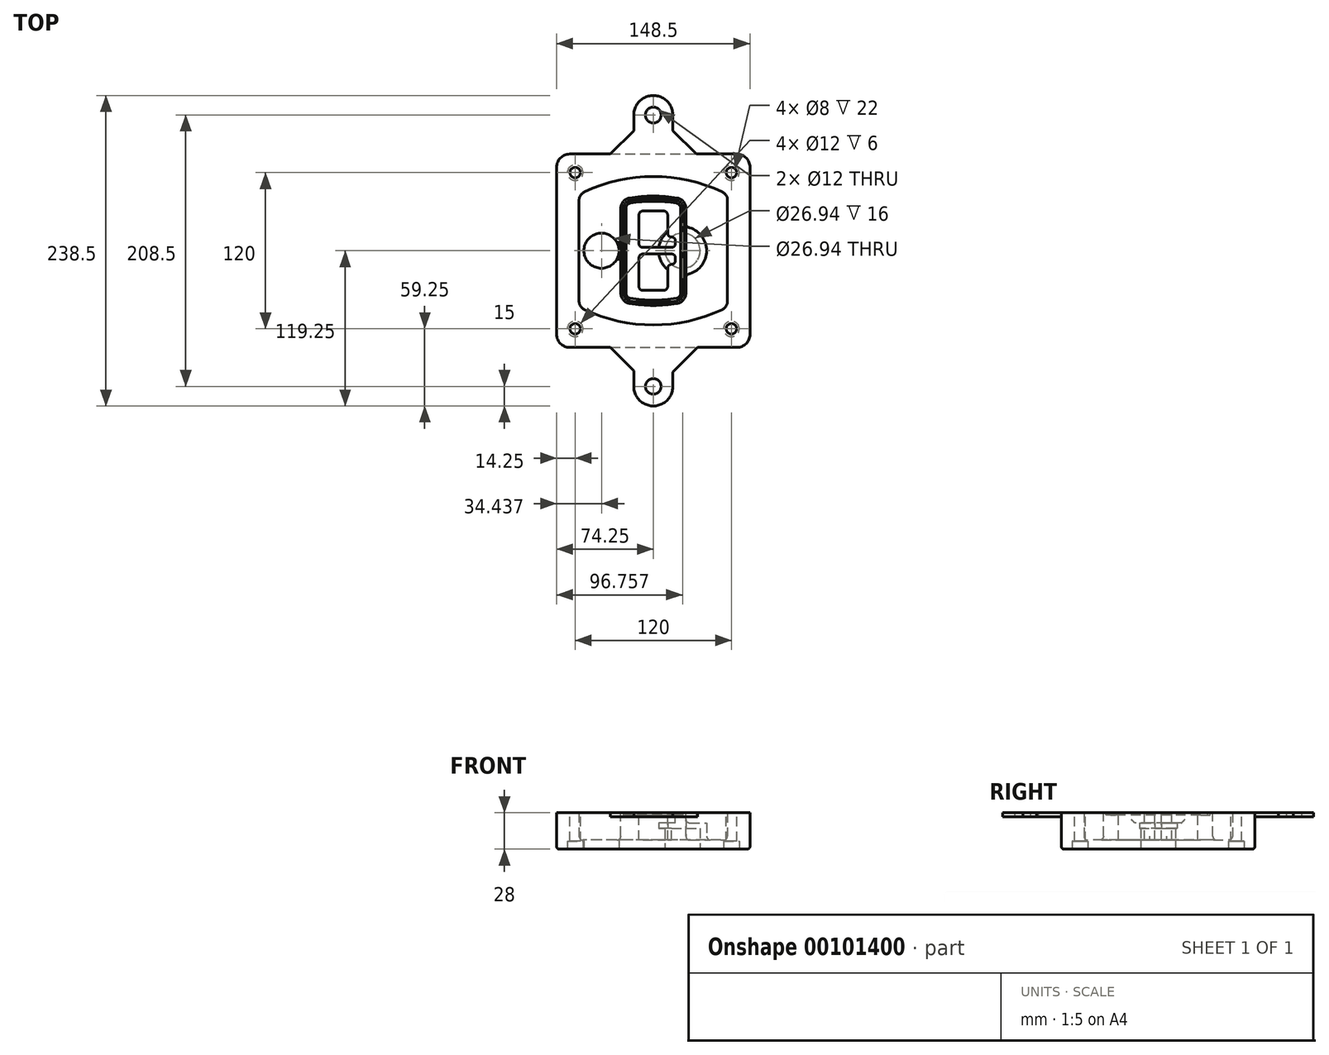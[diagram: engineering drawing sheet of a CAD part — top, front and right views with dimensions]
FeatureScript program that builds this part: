
annotation { "Feature Type Name" : "Feature", "Feature Type Description" : "" }
export const myFeature = defineFeature(function(context is Context, id is Id, definition is map)
    precondition{}
    {
        {
            var Q0;
            Q0=qCreatedBy(makeId("Top.planeOp"),FACE);
            var sketch = newSketch(context, id + "F0", { "sketchPlane" : qUnion([Q0])});
            skPoint(sketch, "E0.rect.middle", {"position": v(0, 0) * mm});
            skLineSegment(sketch, "E1.bottom", {"start": v(-64.25, -74.25) * mm, "end": v(64.25, -74.25) * mm});
            skLineSegment(sketch, "E1.top", {"start": v(-64.25, 74.25) * mm, "end": v(64.25, 74.25) * mm});
            skLineSegment(sketch, "E1.left", {"start": v(-74.25, -64.25) * mm, "end": v(-74.25, 64.25) * mm});
            skLineSegment(sketch, "E1.right", {"start": v(74.25, -64.25) * mm, "end": v(74.25, 64.25) * mm});
            skLineSegment(sketch, "E2", {"start": v(-74.25, 74.25) * mm, "end": v(74.25, -74.25) * mm, "construction": true});
            skLineSegment(sketch, "E3", {"start": v(74.25, 74.25) * mm, "end": v(-74.25, -74.25) * mm, "construction": true});
            skCircle(sketch, "E4", {"center": v(-60, 60) * mm, "radius": 4 * mm});
            skCircle(sketch, "E5", {"center": v(60, 60) * mm, "radius": 4 * mm});
            skCircle(sketch, "E6", {"center": v(60, -60) * mm, "radius": 4 * mm});
            skCircle(sketch, "E7", {"center": v(-60, -60) * mm, "radius": 4 * mm});
            skLineSegment(sketch, "E8", {"start": v(-60, 60) * mm, "end": v(60, 60) * mm, "construction": true});
            skLineSegment(sketch, "E9", {"start": v(60, 60) * mm, "end": v(60, -60) * mm, "construction": true});
            skLineSegment(sketch, "E10", {"start": v(60, -60) * mm, "end": v(-60, -60) * mm, "construction": true});
            skLineSegment(sketch, "E11", {"start": v(-60, -60) * mm, "end": v(-60, 60) * mm, "construction": true});
            skLineSegment(sketch, "E12", {"start": v(-60, 38.83) * mm, "end": v(-60, -38.83) * mm});
            skLineSegment(sketch, "E13", {"start": v(60, 38.83) * mm, "end": v(60, -38.83) * mm});
            skArc(sketch, "E14", {"start": v(54.26, 47.88) * mm, "mid": v(0, 60) * mm, "end": v(-54.26, 47.88) * mm});
            skArc(sketch, "E15", {"start": v(-54.26, -47.88) * mm, "mid": v(0, -60) * mm, "end": v(54.26, -47.88) * mm});
            skLineSegment(sketch, "E16", {"start": v(-60, 0) * mm, "end": v(60, 0) * mm, "construction": true});
            skPoint(sketch, "E17.visualSharp", {"position": v(-60, -45) * mm});
            skArc(sketch, "E17.filletArc", {"start": v(-60, -38.83) * mm, "mid": v(-58.44, -44.2) * mm, "end": v(-54.26, -47.88) * mm});
            skPoint(sketch, "E18.visualSharp", {"position": v(-60, 45) * mm});
            skArc(sketch, "E18.filletArc", {"start": v(-54.26, 47.88) * mm, "mid": v(-58.44, 44.2) * mm, "end": v(-60, 38.83) * mm});
            skPoint(sketch, "E19.visualSharp", {"position": v(60, 45) * mm});
            skArc(sketch, "E19.filletArc", {"start": v(60, 38.83) * mm, "mid": v(58.44, 44.2) * mm, "end": v(54.26, 47.88) * mm});
            skPoint(sketch, "E20.visualSharp", {"position": v(60, -45) * mm});
            skArc(sketch, "E20.filletArc", {"start": v(54.26, -47.88) * mm, "mid": v(58.44, -44.2) * mm, "end": v(60, -38.83) * mm});
            skPoint(sketch, "E21.visualSharp", {"position": v(-74.25, 74.25) * mm});
            skArc(sketch, "E21.filletArc", {"start": v(-64.25, 74.25) * mm, "mid": v(-71.32, 71.32) * mm, "end": v(-74.25, 64.25) * mm});
            skPoint(sketch, "E22.visualSharp", {"position": v(74.25, 74.25) * mm});
            skArc(sketch, "E22.filletArc", {"start": v(74.25, 64.25) * mm, "mid": v(71.32, 71.32) * mm, "end": v(64.25, 74.25) * mm});
            skPoint(sketch, "E23.visualSharp", {"position": v(74.25, -74.25) * mm});
            skArc(sketch, "E23.filletArc", {"start": v(64.25, -74.25) * mm, "mid": v(71.32, -71.32) * mm, "end": v(74.25, -64.25) * mm});
            skPoint(sketch, "E24.visualSharp", {"position": v(-74.25, -74.25) * mm});
            skArc(sketch, "E24.filletArc", {"start": v(-74.25, -64.25) * mm, "mid": v(-71.32, -71.32) * mm, "end": v(-64.25, -74.25) * mm});
            skArc(sketch, "E25.0", {"start": v(57, 38.83) * mm, "mid": v(55.9, 42.58) * mm, "end": v(52.98, 45.17) * mm});
            skLineSegment(sketch, "E25.1", {"start": v(57, 38.83) * mm, "end": v(57, -38.83) * mm});
            skArc(sketch, "E25.2", {"start": v(52.98, -45.17) * mm, "mid": v(55.9, -42.58) * mm, "end": v(57, -38.83) * mm});
            skArc(sketch, "E25.3", {"start": v(-52.98, -45.17) * mm, "mid": v(0, -57) * mm, "end": v(52.98, -45.17) * mm});
            skArc(sketch, "E25.4", {"start": v(-57, -38.83) * mm, "mid": v(-55.9, -42.58) * mm, "end": v(-52.98, -45.17) * mm});
            skArc(sketch, "E25.5", {"start": v(52.98, 45.17) * mm, "mid": v(0, 57) * mm, "end": v(-52.98, 45.17) * mm});
            skLineSegment(sketch, "E25.6", {"start": v(-57, 38.83) * mm, "end": v(-57, -38.83) * mm});
            skArc(sketch, "E25.7", {"start": v(-52.98, 45.17) * mm, "mid": v(-55.9, 42.58) * mm, "end": v(-57, 38.83) * mm});
            skArc(sketch, "E26.0", {"start": v(-55.96, 51.5) * mm, "mid": v(-61.82, 46.33) * mm, "end": v(-64, 38.83) * mm});
            skArc(sketch, "E26.1", {"start": v(55.96, 51.5) * mm, "mid": v(0, 64) * mm, "end": v(-55.96, 51.5) * mm});
            skArc(sketch, "E26.2", {"start": v(64, 38.83) * mm, "mid": v(61.82, 46.33) * mm, "end": v(55.96, 51.5) * mm});
            skLineSegment(sketch, "E26.3", {"start": v(64, 38.83) * mm, "end": v(64, -38.83) * mm});
            skArc(sketch, "E26.4", {"start": v(55.96, -51.5) * mm, "mid": v(61.82, -46.33) * mm, "end": v(64, -38.83) * mm});
            skLineSegment(sketch, "E26.5", {"start": v(-64, 38.83) * mm, "end": v(-64, -38.83) * mm});
            skArc(sketch, "E26.6", {"start": v(-55.96, -51.5) * mm, "mid": v(0, -64) * mm, "end": v(55.96, -51.5) * mm});
            skArc(sketch, "E26.7", {"start": v(-64, -38.83) * mm, "mid": v(-61.82, -46.33) * mm, "end": v(-55.96, -51.5) * mm});
            skSolve(sketch);
        }
        {
            var Q0;
            Q0=makeQuery(id+"F0.imprint","IMPRINT",FACE,{"disambiguationData":[TD([[makeQuery(id+"F0.imprint","IMPRINT",EDGE,{"derivedFrom":sQuery(id+"F0.wireOp",EDGE,"E1.bottom")}),1.0]])]});
            var Q1;
            Q1=makeQuery(id+"F0.imprint","IMPRINT",FACE,{"disambiguationData":[TD([[makeQuery(id+"F0.imprint","IMPRINT",EDGE,{"derivedFrom":sQuery(id+"F0.wireOp",EDGE,"E12")}),1.0]])]});
            var Q2;
            Q2=makeQuery(id+"F0.imprint","IMPRINT",FACE,{"disambiguationData":[TD([[makeQuery(id+"F0.imprint","IMPRINT",EDGE,{"derivedFrom":sQuery(id+"F0.wireOp",EDGE,"E25.0")}),1.0]])]});
            var Q3;
            Q3=makeQuery(id+"F0.imprint","IMPRINT",FACE,{"disambiguationData":[TD([[makeQuery(id+"F0.imprint","IMPRINT",EDGE,{"derivedFrom":sQuery(id+"F0.wireOp",EDGE,"E12")}),-1.0]])]});
            extrude(context, id + "F1", {"entities" : qUnion([Q0, Q1, Q2, Q3]), "oppositeDirection" : true, "depth" : 25 * mm});
        }
        {
            var Q0;
            Q0=makeQuery(id+"F0.imprint","IMPRINT",FACE,{"disambiguationData":[TD([[makeQuery(id+"F0.imprint","IMPRINT",EDGE,{"derivedFrom":sQuery(id+"F0.wireOp",EDGE,"E12")}),1.0]])]});
            extrude(context, id + "F2", {"entities" : qUnion([Q0]), "operationType" : NewBodyOperationType.ADD, "depth" : 3 * mm});
        }
        {
            var Q0;
            Q0=makeQuery(id+"F0.imprint","IMPRINT",FACE,{"disambiguationData":[TD([[makeQuery(id+"F0.imprint","IMPRINT",EDGE,{"derivedFrom":sQuery(id+"F0.wireOp",EDGE,"E25.0")}),1.0]])]});
            extrude(context, id + "F3", {"entities" : qUnion([Q0]), "operationType" : NewBodyOperationType.REMOVE, "oppositeDirection" : true, "depth" : 18 * mm});
        }
        {
            var Q0;
            Q0=makeQuery(id+"F2.opExtrude","CAP_FACE",FACE,{"disambiguationData":[OSD([sQuery(id+"F0.wireOp",EDGE,"E12"),sQuery(id+"F0.wireOp",EDGE,"E13"),sQuery(id+"F0.wireOp",EDGE,"E14"),sQuery(id+"F0.wireOp",EDGE,"E15"),sQuery(id+"F0.wireOp",EDGE,"E17.filletArc"),sQuery(id+"F0.wireOp",EDGE,"E18.filletArc"),sQuery(id+"F0.wireOp",EDGE,"E19.filletArc"),sQuery(id+"F0.wireOp",EDGE,"E20.filletArc"),sQuery(id+"F0.wireOp",EDGE,"E25.0"),sQuery(id+"F0.wireOp",EDGE,"E25.1"),sQuery(id+"F0.wireOp",EDGE,"E25.2"),sQuery(id+"F0.wireOp",EDGE,"E25.3"),sQuery(id+"F0.wireOp",EDGE,"E25.4"),sQuery(id+"F0.wireOp",EDGE,"E25.5"),sQuery(id+"F0.wireOp",EDGE,"E25.6"),sQuery(id+"F0.wireOp",EDGE,"E25.7")])],"isStart":false});
            var sketch = newSketch(context, id + "F4", { "sketchPlane" : qUnion([Q0])});
            skArc(sketch, "E27.0", {"start": v(-18.34, -40.45) * mm, "mid": v(0, -42) * mm, "end": v(18.34, -40.45) * mm});
            skArc(sketch, "E28.0", {"start": v(18.34, 40.45) * mm, "mid": v(0, 42) * mm, "end": v(-18.34, 40.45) * mm});
            skLineSegment(sketch, "E29", {"start": v(-25, 32.57) * mm, "end": v(-25, -32.57) * mm});
            skLineSegment(sketch, "E30", {"start": v(25, 32.57) * mm, "end": v(25, -32.57) * mm});
            skLineSegment(sketch, "E31", {"start": v(-25, 39.1) * mm, "end": v(25, 39.1) * mm, "construction": true});
            skLineSegment(sketch, "E32", {"start": v(-25, -39.1) * mm, "end": v(25, -39.1) * mm, "construction": true});
            skPoint(sketch, "E33.visualSharp", {"position": v(-25, 39.1) * mm});
            skArc(sketch, "E33.filletArc", {"start": v(-18.34, 40.45) * mm, "mid": v(-23.11, 37.73) * mm, "end": v(-25, 32.57) * mm});
            skPoint(sketch, "E34.visualSharp", {"position": v(25, 39.1) * mm});
            skArc(sketch, "E34.filletArc", {"start": v(25, 32.57) * mm, "mid": v(23.11, 37.73) * mm, "end": v(18.34, 40.45) * mm});
            skPoint(sketch, "E35.visualSharp", {"position": v(25, -39.1) * mm});
            skArc(sketch, "E35.filletArc", {"start": v(18.34, -40.45) * mm, "mid": v(23.11, -37.73) * mm, "end": v(25, -32.57) * mm});
            skPoint(sketch, "E36.visualSharp", {"position": v(-25, -39.1) * mm});
            skArc(sketch, "E36.filletArc", {"start": v(-25, -32.57) * mm, "mid": v(-23.11, -37.73) * mm, "end": v(-18.34, -40.45) * mm});
            skArc(sketch, "E37.0", {"start": v(52.98, 45.17) * mm, "mid": v(0, 57) * mm, "end": v(-52.98, 45.17) * mm});
            skArc(sketch, "E37.1", {"start": v(-52.98, 45.17) * mm, "mid": v(-55.9, 42.58) * mm, "end": v(-57, 38.83) * mm});
            skLineSegment(sketch, "E37.2", {"start": v(-57, 38.83) * mm, "end": v(-57, -38.83) * mm});
            skArc(sketch, "E37.3", {"start": v(-57, -38.83) * mm, "mid": v(-55.9, -42.58) * mm, "end": v(-52.98, -45.17) * mm});
            skArc(sketch, "E37.4", {"start": v(-52.98, -45.17) * mm, "mid": v(0, -57) * mm, "end": v(52.98, -45.17) * mm});
            skArc(sketch, "E37.5", {"start": v(52.98, -45.17) * mm, "mid": v(55.9, -42.58) * mm, "end": v(57, -38.83) * mm});
            skLineSegment(sketch, "E37.6", {"start": v(57, 38.83) * mm, "end": v(57, -38.83) * mm});
            skArc(sketch, "E37.7", {"start": v(57, 38.83) * mm, "mid": v(55.9, 42.58) * mm, "end": v(52.98, 45.17) * mm});
            skLineSegment(sketch, "E38.0", {"start": v(23, 32.57) * mm, "end": v(23, -32.57) * mm});
            skArc(sketch, "E38.1", {"start": v(18, -38.48) * mm, "mid": v(21.58, -36.44) * mm, "end": v(23, -32.57) * mm});
            skArc(sketch, "E38.2", {"start": v(-18, -38.48) * mm, "mid": v(0, -40) * mm, "end": v(18, -38.48) * mm});
            skArc(sketch, "E38.3", {"start": v(-23, -32.57) * mm, "mid": v(-21.58, -36.44) * mm, "end": v(-18, -38.48) * mm});
            skLineSegment(sketch, "E38.4", {"start": v(-23, 32.57) * mm, "end": v(-23, -32.57) * mm});
            skArc(sketch, "E38.5", {"start": v(23, 32.57) * mm, "mid": v(21.58, 36.44) * mm, "end": v(18, 38.48) * mm});
            skArc(sketch, "E38.6", {"start": v(-18, 38.48) * mm, "mid": v(-21.58, 36.44) * mm, "end": v(-23, 32.57) * mm});
            skArc(sketch, "E38.7", {"start": v(18, 38.48) * mm, "mid": v(0, 40) * mm, "end": v(-18, 38.48) * mm});
            skArc(sketch, "E39.0", {"start": v(21, 32.57) * mm, "mid": v(20.06, 35.15) * mm, "end": v(17.67, 36.5) * mm});
            skLineSegment(sketch, "E39.1", {"start": v(21, 32.57) * mm, "end": v(21, -32.57) * mm});
            skArc(sketch, "E39.2", {"start": v(17.67, -36.5) * mm, "mid": v(20.06, -35.15) * mm, "end": v(21, -32.57) * mm});
            skArc(sketch, "E39.3", {"start": v(-17.67, -36.5) * mm, "mid": v(0, -38) * mm, "end": v(17.67, -36.5) * mm});
            skArc(sketch, "E39.4", {"start": v(-21, -32.57) * mm, "mid": v(-20.06, -35.15) * mm, "end": v(-17.67, -36.5) * mm});
            skArc(sketch, "E39.5", {"start": v(17.67, 36.5) * mm, "mid": v(0, 38) * mm, "end": v(-17.67, 36.5) * mm});
            skLineSegment(sketch, "E39.6", {"start": v(-21, 32.57) * mm, "end": v(-21, -32.57) * mm});
            skArc(sketch, "E39.7", {"start": v(-17.67, 36.5) * mm, "mid": v(-20.06, 35.15) * mm, "end": v(-21, 32.57) * mm});
            skLineSegment(sketch, "E40", {"start": v(-25, 0) * mm, "end": v(25, 0) * mm, "construction": true});
            skLineSegment(sketch, "E41", {"start": v(-11, 5.5) * mm, "end": v(-11, 27.5) * mm});
            skLineSegment(sketch, "E42", {"start": v(-8, 30.5) * mm, "end": v(8, 30.5) * mm});
            skLineSegment(sketch, "E43", {"start": v(11, 27.5) * mm, "end": v(11, 13.5) * mm});
            skLineSegment(sketch, "E44", {"start": v(14, 10.5) * mm, "end": v(14, 10.5) * mm});
            skLineSegment(sketch, "E45", {"start": v(17, 7.5) * mm, "end": v(17, 5.5) * mm});
            skLineSegment(sketch, "E46", {"start": v(14, 2.5) * mm, "end": v(-8, 2.5) * mm});
            skPoint(sketch, "E47.visualSharp", {"position": v(-11, 30.5) * mm});
            skArc(sketch, "E47.filletArc", {"start": v(-8, 30.5) * mm, "mid": v(-10.12, 29.62) * mm, "end": v(-11, 27.5) * mm});
            skPoint(sketch, "E48.visualSharp", {"position": v(11, 30.5) * mm});
            skArc(sketch, "E48.filletArc", {"start": v(11, 27.5) * mm, "mid": v(10.12, 29.62) * mm, "end": v(8, 30.5) * mm});
            skPoint(sketch, "E49.visualSharp", {"position": v(11, 10.5) * mm});
            skArc(sketch, "E49.filletArc", {"start": v(11, 13.5) * mm, "mid": v(11.88, 11.38) * mm, "end": v(14, 10.5) * mm});
            skPoint(sketch, "E50.visualSharp", {"position": v(17, 10.5) * mm});
            skArc(sketch, "E50.filletArc", {"start": v(17, 7.5) * mm, "mid": v(16.12, 9.62) * mm, "end": v(14, 10.5) * mm});
            skPoint(sketch, "E51.visualSharp", {"position": v(17, 2.5) * mm});
            skArc(sketch, "E51.filletArc", {"start": v(14, 2.5) * mm, "mid": v(16.12, 3.38) * mm, "end": v(17, 5.5) * mm});
            skPoint(sketch, "E52.visualSharp", {"position": v(-11, 2.5) * mm});
            skArc(sketch, "E52.filletArc", {"start": v(-11, 5.5) * mm, "mid": v(-10.12, 3.38) * mm, "end": v(-8, 2.5) * mm});
            skLineSegment(sketch, "E53.0.MirrorCS", {"start": v(14, -2.5) * mm, "end": v(-8, -2.5) * mm});
            skArc(sketch, "E54.0.MirrorCS", {"start": v(-11, -5.5) * mm, "mid": v(-10.12, -3.38) * mm, "end": v(-8, -2.5) * mm});
            skLineSegment(sketch, "E55.0.MirrorCS", {"start": v(-11, -5.5) * mm, "end": v(-11, -27.5) * mm});
            skArc(sketch, "E56.0.MirrorCS", {"start": v(-8, -30.5) * mm, "mid": v(-10.12, -29.62) * mm, "end": v(-11, -27.5) * mm});
            skLineSegment(sketch, "E57.0.MirrorCS", {"start": v(-8, -30.5) * mm, "end": v(8, -30.5) * mm});
            skArc(sketch, "E58.0.MirrorCS", {"start": v(11, -27.5) * mm, "mid": v(10.12, -29.62) * mm, "end": v(8, -30.5) * mm});
            skLineSegment(sketch, "E59.0.MirrorCS", {"start": v(11, -27.5) * mm, "end": v(11, -13.5) * mm});
            skArc(sketch, "E60.0.MirrorCS", {"start": v(11, -13.5) * mm, "mid": v(11.88, -11.38) * mm, "end": v(14, -10.5) * mm});
            skArc(sketch, "E61.0.MirrorCS", {"start": v(17, -7.5) * mm, "mid": v(16.12, -9.62) * mm, "end": v(14, -10.5) * mm});
            skLineSegment(sketch, "E62.0.MirrorCS", {"start": v(17, -7.5) * mm, "end": v(17, -5.5) * mm});
            skArc(sketch, "E63.0.MirrorCS", {"start": v(14, -2.5) * mm, "mid": v(16.12, -3.38) * mm, "end": v(17, -5.5) * mm});
            skSolve(sketch);
        }
        {
            var Q0;
            Q0=makeQuery(id+"F4.imprint","IMPRINT",FACE,{"disambiguationData":[TD([[makeQuery(id+"F4.imprint","IMPRINT",EDGE,{"derivedFrom":sQuery(id+"F4.wireOp",EDGE,"E27.0")}),1.0]])]});
            var Q1;
            Q1=makeQuery(id+"F4.imprint","IMPRINT",FACE,{"disambiguationData":[TD([[makeQuery(id+"F4.imprint","IMPRINT",EDGE,{"derivedFrom":sQuery(id+"F4.wireOp",EDGE,"E38.0")}),-1.0]])]});
            var Q2;
            Q2=makeQuery(id+"F4.imprint","IMPRINT",FACE,{"disambiguationData":[TD([[makeQuery(id+"F4.imprint","IMPRINT",EDGE,{"derivedFrom":sQuery(id+"F4.wireOp",EDGE,"E39.0")}),1.0]])]});
            extrude(context, id + "F5", {"entities" : qUnion([Q0, Q1, Q2]), "operationType" : NewBodyOperationType.ADD, "endBound" : BoundingType.UP_TO_NEXT, "oppositeDirection" : true, "depth" : 25 * mm});
        }
        {
            var Q0;
            Q0=makeQuery(id+"F4.imprint","IMPRINT",FACE,{"disambiguationData":[TD([[makeQuery(id+"F4.imprint","IMPRINT",EDGE,{"derivedFrom":sQuery(id+"F4.wireOp",EDGE,"E38.0")}),-1.0]])]});
            extrude(context, id + "F6", {"entities" : qUnion([Q0]), "operationType" : NewBodyOperationType.REMOVE, "oppositeDirection" : true, "depth" : 2 * mm});
        }
        {
            var Q0;
            Q0=makeQuery(id+"F1.opExtrude","CAP_FACE",FACE,{"disambiguationData":[OSD([sQuery(id+"F0.wireOp",EDGE,"E1.bottom"),sQuery(id+"F0.wireOp",EDGE,"E1.top"),sQuery(id+"F0.wireOp",EDGE,"E1.left"),sQuery(id+"F0.wireOp",EDGE,"E1.right"),sQuery(id+"F0.wireOp",EDGE,"E4"),sQuery(id+"F0.wireOp",EDGE,"E5"),sQuery(id+"F0.wireOp",EDGE,"E6"),sQuery(id+"F0.wireOp",EDGE,"E7"),sQuery(id+"F0.wireOp",EDGE,"E21.filletArc"),sQuery(id+"F0.wireOp",EDGE,"E22.filletArc"),sQuery(id+"F0.wireOp",EDGE,"E23.filletArc"),sQuery(id+"F0.wireOp",EDGE,"E24.filletArc")])],"isStart":false});
            var sketch = newSketch(context, id + "F7", { "sketchPlane" : qUnion([Q0])});
            skCircle(sketch, "E64", {"center": v(22.5, 0) * mm, "radius": 13.47 * mm});
            skCircle(sketch, "E65", {"center": v(-39.81, 0) * mm, "radius": 13.47 * mm});
            skLineSegment(sketch, "E66", {"start": v(74.25, 0) * mm, "end": v(-74.25, 0) * mm});
            skCircle(sketch, "E67", {"center": v(22.5, 0) * mm, "radius": 18.47 * mm});
            skCircle(sketch, "E68", {"center": v(60, -60) * mm, "radius": 6 * mm});
            skCircle(sketch, "E69", {"center": v(-60, -60) * mm, "radius": 6 * mm});
            skCircle(sketch, "E70", {"center": v(-60, 60) * mm, "radius": 6 * mm});
            skCircle(sketch, "E71", {"center": v(60, 60) * mm, "radius": 6 * mm});
            skSolve(sketch);
        }
        {
            var Q0;
            {var subQ1=sQuery(id+"F7.wireOp",EDGE,"E66");var subQ4=sQuery(id+"F7.wireOp",EDGE,"E64");var subQ6=makeQuery(id+"F7.imprint","INTERSECT",VERTEX,{"disambiguationData":[OD(0.0)],"derivedFrom":[subQ4,subQ1]});Q0=makeQuery(id+"F7.imprint","IMPRINT",FACE,{"disambiguationData":[TD([[makeQuery(id+"F7.imprint","IMPRINT",EDGE,{"disambiguationData":[TD([[subQ6,-1.0]])],"derivedFrom":subQ4}),-1.0]])]});}
            var Q1;
            {var subQ0=sQuery(id+"F7.wireOp",EDGE,"E66");var subQ1=sQuery(id+"F7.wireOp",EDGE,"E64");var subQ3=makeQuery(id+"F7.imprint","INTERSECT",VERTEX,{"disambiguationData":[OD(0.0)],"derivedFrom":[subQ1,subQ0]});Q1=makeQuery(id+"F7.imprint","IMPRINT",FACE,{"disambiguationData":[TD([[makeQuery(id+"F7.imprint","IMPRINT",EDGE,{"disambiguationData":[TD([[subQ3,-1.0]])],"derivedFrom":subQ1}),1.0]])]});}
            var Q2;
            {var subQ0=sQuery(id+"F7.wireOp",EDGE,"E66");var subQ1=sQuery(id+"F7.wireOp",EDGE,"E64");var subQ3=makeQuery(id+"F7.imprint","INTERSECT",VERTEX,{"disambiguationData":[OD(0.0)],"derivedFrom":[subQ1,subQ0]});Q2=makeQuery(id+"F7.imprint","IMPRINT",FACE,{"disambiguationData":[TD([[makeQuery(id+"F7.imprint","IMPRINT",EDGE,{"disambiguationData":[TD([[subQ3,1.0]])],"derivedFrom":subQ1}),1.0]])]});}
            var Q3;
            {var subQ1=sQuery(id+"F7.wireOp",EDGE,"E66");var subQ4=sQuery(id+"F7.wireOp",EDGE,"E64");var subQ6=makeQuery(id+"F7.imprint","INTERSECT",VERTEX,{"disambiguationData":[OD(0.0)],"derivedFrom":[subQ4,subQ1]});Q3=makeQuery(id+"F7.imprint","IMPRINT",FACE,{"disambiguationData":[TD([[makeQuery(id+"F7.imprint","IMPRINT",EDGE,{"disambiguationData":[TD([[subQ6,1.0]])],"derivedFrom":subQ4}),-1.0]])]});}
            extrude(context, id + "F8", {"entities" : qUnion([Q0, Q1, Q2, Q3]), "operationType" : NewBodyOperationType.ADD, "oppositeDirection" : true, "depth" : 20 * mm});
        }
        {
            var Q0;
            {var subQ0=sQuery(id+"F7.wireOp",EDGE,"E66");var subQ1=sQuery(id+"F7.wireOp",EDGE,"E64");var subQ3=makeQuery(id+"F7.imprint","INTERSECT",VERTEX,{"disambiguationData":[OD(0.0)],"derivedFrom":[subQ1,subQ0]});Q0=makeQuery(id+"F7.imprint","IMPRINT",FACE,{"disambiguationData":[TD([[makeQuery(id+"F7.imprint","IMPRINT",EDGE,{"disambiguationData":[TD([[subQ3,-1.0]])],"derivedFrom":subQ1}),1.0]])]});}
            var Q1;
            {var subQ0=sQuery(id+"F7.wireOp",EDGE,"E66");var subQ1=sQuery(id+"F7.wireOp",EDGE,"E64");var subQ3=makeQuery(id+"F7.imprint","INTERSECT",VERTEX,{"disambiguationData":[OD(0.0)],"derivedFrom":[subQ1,subQ0]});Q1=makeQuery(id+"F7.imprint","IMPRINT",FACE,{"disambiguationData":[TD([[makeQuery(id+"F7.imprint","IMPRINT",EDGE,{"disambiguationData":[TD([[subQ3,1.0]])],"derivedFrom":subQ1}),1.0]])]});}
            extrude(context, id + "F9", {"entities" : qUnion([Q0, Q1]), "operationType" : NewBodyOperationType.REMOVE, "oppositeDirection" : true, "depth" : 16 * mm});
        }
        {
            var Q0;
            {var subQ0=sQuery(id+"F7.wireOp",EDGE,"E66");var subQ1=sQuery(id+"F7.wireOp",EDGE,"E65");var subQ3=makeQuery(id+"F7.imprint","INTERSECT",VERTEX,{"disambiguationData":[OD(0.0)],"derivedFrom":[subQ1,subQ0]});Q0=makeQuery(id+"F7.imprint","IMPRINT",FACE,{"disambiguationData":[TD([[makeQuery(id+"F7.imprint","IMPRINT",EDGE,{"disambiguationData":[TD([[subQ3,-1.0]])],"derivedFrom":subQ1}),1.0]])]});}
            var Q1;
            {var subQ0=sQuery(id+"F7.wireOp",EDGE,"E66");var subQ1=sQuery(id+"F7.wireOp",EDGE,"E65");var subQ3=makeQuery(id+"F7.imprint","INTERSECT",VERTEX,{"disambiguationData":[OD(0.0)],"derivedFrom":[subQ1,subQ0]});Q1=makeQuery(id+"F7.imprint","IMPRINT",FACE,{"disambiguationData":[TD([[makeQuery(id+"F7.imprint","IMPRINT",EDGE,{"disambiguationData":[TD([[subQ3,1.0]])],"derivedFrom":subQ1}),1.0]])]});}
            extrude(context, id + "F10", {"entities" : qUnion([Q0, Q1]), "operationType" : NewBodyOperationType.REMOVE, "oppositeDirection" : true, "depth" : 25 * mm});
        }
        {
            var Q0;
            Q0=makeQuery(id+"F7.imprint","IMPRINT",FACE,{"disambiguationData":[TD([[makeQuery(id+"F7.imprint","IMPRINT",EDGE,{"derivedFrom":sQuery(id+"F7.wireOp",EDGE,"E68")}),1.0]])]});
            var Q1;
            Q1=makeQuery(id+"F7.imprint","IMPRINT",FACE,{"disambiguationData":[TD([[makeQuery(id+"F7.imprint","IMPRINT",EDGE,{"derivedFrom":makeQuery(id+"F1.opExtrude","CAP_EDGE",EDGE,{"disambiguationData":[OSD([sQuery(id+"F0.wireOp",EDGE,"E5")])],"isStart":false})}),-1.0]])]});
            var Q2;
            Q2=makeQuery(id+"F7.imprint","IMPRINT",FACE,{"disambiguationData":[TD([[makeQuery(id+"F7.imprint","IMPRINT",EDGE,{"derivedFrom":sQuery(id+"F7.wireOp",EDGE,"E69")}),1.0]])]});
            var Q3;
            Q3=makeQuery(id+"F7.imprint","IMPRINT",FACE,{"disambiguationData":[TD([[makeQuery(id+"F7.imprint","IMPRINT",EDGE,{"derivedFrom":makeQuery(id+"F1.opExtrude","CAP_EDGE",EDGE,{"disambiguationData":[OSD([sQuery(id+"F0.wireOp",EDGE,"E4")])],"isStart":false})}),-1.0]])]});
            var Q4;
            Q4=makeQuery(id+"F7.imprint","IMPRINT",FACE,{"disambiguationData":[TD([[makeQuery(id+"F7.imprint","IMPRINT",EDGE,{"derivedFrom":sQuery(id+"F7.wireOp",EDGE,"E70")}),1.0]])]});
            var Q5;
            Q5=makeQuery(id+"F7.imprint","IMPRINT",FACE,{"disambiguationData":[TD([[makeQuery(id+"F7.imprint","IMPRINT",EDGE,{"derivedFrom":makeQuery(id+"F1.opExtrude","CAP_EDGE",EDGE,{"disambiguationData":[OSD([sQuery(id+"F0.wireOp",EDGE,"E7")])],"isStart":false})}),-1.0]])]});
            var Q6;
            Q6=makeQuery(id+"F7.imprint","IMPRINT",FACE,{"disambiguationData":[TD([[makeQuery(id+"F7.imprint","IMPRINT",EDGE,{"derivedFrom":sQuery(id+"F7.wireOp",EDGE,"E71")}),1.0]])]});
            var Q7;
            Q7=makeQuery(id+"F7.imprint","IMPRINT",FACE,{"disambiguationData":[TD([[makeQuery(id+"F7.imprint","IMPRINT",EDGE,{"derivedFrom":makeQuery(id+"F1.opExtrude","CAP_EDGE",EDGE,{"disambiguationData":[OSD([sQuery(id+"F0.wireOp",EDGE,"E6")])],"isStart":false})}),-1.0]])]});
            extrude(context, id + "F11", {"entities" : qUnion([Q0, Q1, Q2, Q3, Q4, Q5, Q6, Q7]), "operationType" : NewBodyOperationType.REMOVE, "oppositeDirection" : true, "depth" : 6 * mm});
        }
        {
            var Q0;
            Q0=makeQuery(id+"F9.boolean.opBoolean","COPY",FACE,{"derivedFrom":makeQuery(id+"F9.opExtrude","CAP_FACE",FACE,{"disambiguationData":[OSD([sQuery(id+"F7.wireOp",EDGE,"E64")])],"isStart":false})});
            var sketch = newSketch(context, id + "F12", { "sketchPlane" : qUnion([Q0])});
            skArc(sketch, "E72.0", {"start": v(11, 14.45) * mm, "mid": v(6.45, 9.13) * mm, "end": v(4.2, 2.5) * mm});
            skArc(sketch, "E72.1", {"start": v(4.2, -2.5) * mm, "mid": v(6.45, -9.13) * mm, "end": v(11, -14.45) * mm});
            skLineSegment(sketch, "E73", {"start": v(4.2, -2.5) * mm, "end": v(14, -2.5) * mm});
            skLineSegment(sketch, "E74.0", {"start": v(14, 2.5) * mm, "end": v(4.2, 2.5) * mm});
            skArc(sketch, "E74.1", {"start": v(14, 2.5) * mm, "mid": v(16.12, 3.38) * mm, "end": v(17, 5.5) * mm});
            skLineSegment(sketch, "E74.2", {"start": v(17, 7.5) * mm, "end": v(17, 5.5) * mm});
            skArc(sketch, "E74.3", {"start": v(17, 7.5) * mm, "mid": v(16.12, 9.62) * mm, "end": v(14, 10.5) * mm});
            skArc(sketch, "E74.4", {"start": v(11, 13.5) * mm, "mid": v(11.88, 11.38) * mm, "end": v(14, 10.5) * mm});
            skLineSegment(sketch, "E74.5", {"start": v(11, 14.45) * mm, "end": v(11, 13.5) * mm});
            skLineSegment(sketch, "E74.7", {"start": v(14, -2.5) * mm, "end": v(4.2, -2.5) * mm});
            skArc(sketch, "E74.8", {"start": v(14, -2.5) * mm, "mid": v(16.12, -3.38) * mm, "end": v(17, -5.5) * mm});
            skLineSegment(sketch, "E74.9", {"start": v(17, -7.5) * mm, "end": v(17, -5.5) * mm});
            skArc(sketch, "E74.10", {"start": v(17, -7.5) * mm, "mid": v(16.12, -9.62) * mm, "end": v(14, -10.5) * mm});
            skArc(sketch, "E74.11", {"start": v(11, -13.5) * mm, "mid": v(11.88, -11.38) * mm, "end": v(14, -10.5) * mm});
            skLineSegment(sketch, "E74.12", {"start": v(11, -14.45) * mm, "end": v(11, -13.5) * mm});
            skPoint(sketch, "E75.orphan", {"position": v(11, -27.5) * mm});
            skPoint(sketch, "E76.orphan", {"position": v(-8, -2.5) * mm});
            skPoint(sketch, "E77.orphan", {"position": v(-8, 2.5) * mm});
            skPoint(sketch, "E78.orphan", {"position": v(11, 27.5) * mm});
            skSolve(sketch);
        }
        {
            var Q0;
            {var subQ7=sQuery(id+"F12.wireOp",EDGE,"E72.0");var subQ14=sQuery(id+"F12.wireOp",EDGE,"E72.1");var subQ16=sQuery(id+"F12.wireOp",EDGE,"E74.1");var subQ18=sQuery(id+"F12.wireOp",EDGE,"E74.8");Q0=qUnion([makeQuery(id+"F12.imprint","IMPRINT",FACE,{"disambiguationData":[TD([[makeQuery(id+"F12.imprint","IMPRINT",EDGE,{"derivedFrom":subQ7}),1.0]])]}),makeQuery(id+"F12.imprint","IMPRINT",FACE,{"disambiguationData":[TD([[makeQuery(id+"F12.imprint","IMPRINT",EDGE,{"derivedFrom":subQ14}),1.0]])]}),makeQuery(id+"F12.imprint","IMPRINT",FACE,{"disambiguationData":[TD([[makeQuery(id+"F12.imprint","IMPRINT",EDGE,{"derivedFrom":subQ16}),1.0]])]}),makeQuery(id+"F12.imprint","IMPRINT",FACE,{"disambiguationData":[TD([[makeQuery(id+"F12.imprint","IMPRINT",EDGE,{"derivedFrom":subQ18}),-1.0]])]})]);}
            var Q1;
            Q1=makeQuery(id+"F5.boolean.opBoolean","SPLIT",FACE,{"disambiguationData":[TD([makeQuery(id+"F5.opExtrude","SWEPT_FACE",FACE,{"disambiguationData":[OSD([sQuery(id+"F4.wireOp",EDGE,"E41")])]})])],"derivedFrom":makeQuery(id+"F3.boolean.opBoolean","COPY",FACE,{"derivedFrom":makeQuery(id+"F3.opExtrude","CAP_FACE",FACE,{"disambiguationData":[OSD([sQuery(id+"F0.wireOp",EDGE,"E25.0"),sQuery(id+"F0.wireOp",EDGE,"E25.1"),sQuery(id+"F0.wireOp",EDGE,"E25.2"),sQuery(id+"F0.wireOp",EDGE,"E25.3"),sQuery(id+"F0.wireOp",EDGE,"E25.4"),sQuery(id+"F0.wireOp",EDGE,"E25.5"),sQuery(id+"F0.wireOp",EDGE,"E25.6"),sQuery(id+"F0.wireOp",EDGE,"E25.7")])],"isStart":false})})});
            extrude(context, id + "F13", {"entities" : qUnion([Q0]), "operationType" : NewBodyOperationType.REMOVE, "endBound" : BoundingType.UP_TO_SURFACE, "endBoundEntityFace" : qUnion([Q1]), "depth" : 25 * mm});
        }
        {
            var Q0;
            Q0=makeQuery(id+"F3.boolean.opBoolean","COPY",EDGE,{"derivedFrom":makeQuery(id+"F3.opExtrude","CAP_EDGE",EDGE,{"disambiguationData":[OSD([sQuery(id+"F0.wireOp",EDGE,"E25.6")])],"isStart":false})});
            var Q1;
            Q1=makeQuery(id+"F8.boolean.opBoolean","INTERSECT",EDGE,{"derivedFrom":[makeQuery(id+"F5.opExtrude","SWEPT_FACE",FACE,{"disambiguationData":[OSD([sQuery(id+"F4.wireOp",EDGE,"E30")])]}),makeQuery(id+"F8.opExtrude","CAP_FACE",FACE,{"disambiguationData":[OSD([sQuery(id+"F7.wireOp",EDGE,"E67")])],"isStart":false})]});
            var Q2;
            Q2=makeQuery(id+"F8.boolean.opBoolean","INTERSECT",EDGE,{"disambiguationData":[OD(1.0)],"derivedFrom":[makeQuery(id+"F5.opExtrude","SWEPT_FACE",FACE,{"disambiguationData":[OSD([sQuery(id+"F4.wireOp",EDGE,"E30")])]}),makeQuery(id+"F8.opExtrude","SWEPT_FACE",FACE,{"disambiguationData":[OSD([sQuery(id+"F7.wireOp",EDGE,"E67")])]})]});
            var Q3;
            {var subQ0=sQuery(id+"F4.wireOp",EDGE,"E30");Q3=makeQuery(id+"F8.boolean.opBoolean","SPLIT",EDGE,{"disambiguationData":[TD([makeQuery(id+"F5.opExtrude","SWEPT_FACE",FACE,{"disambiguationData":[OSD([sQuery(id+"F4.wireOp",EDGE,"E35.filletArc")])]})])],"derivedFrom":makeQuery(id+"F5.opExtrude","CAP_EDGE",EDGE,{"disambiguationData":[OSD([subQ0])],"isStart":false})});}
            var Q4;
            {var subQ0=sQuery(id+"F0.wireOp",EDGE,"E25.7");var subQ1=sQuery(id+"F0.wireOp",EDGE,"E25.1");var subQ2=sQuery(id+"F0.wireOp",EDGE,"E25.6");var subQ3=sQuery(id+"F0.wireOp",EDGE,"E25.5");var subQ4=sQuery(id+"F0.wireOp",EDGE,"E25.4");var subQ5=sQuery(id+"F0.wireOp",EDGE,"E25.0");var subQ6=sQuery(id+"F0.wireOp",EDGE,"E25.2");var subQ7=sQuery(id+"F0.wireOp",EDGE,"E25.3");Q4=makeQuery(id+"F8.boolean.opBoolean","INTERSECT",EDGE,{"derivedFrom":[makeQuery(id+"F5.boolean.opBoolean","SPLIT",FACE,{"disambiguationData":[TD([makeQuery(id+"F2.opExtrude","SWEPT_FACE",FACE,{"disambiguationData":[OSD([subQ5])]})])],"derivedFrom":makeQuery(id+"F3.boolean.opBoolean","COPY",FACE,{"derivedFrom":makeQuery(id+"F3.opExtrude","CAP_FACE",FACE,{"disambiguationData":[OSD([subQ5,subQ1,subQ6,subQ7,subQ4,subQ3,subQ2,subQ0])],"isStart":false})})}),makeQuery(id+"F8.opExtrude","SWEPT_FACE",FACE,{"disambiguationData":[OSD([sQuery(id+"F7.wireOp",EDGE,"E67")])]})]});}
            var Q5;
            Q5=makeQuery(id+"F8.boolean.opBoolean","INTERSECT",EDGE,{"disambiguationData":[OD(0.0)],"derivedFrom":[makeQuery(id+"F5.opExtrude","SWEPT_FACE",FACE,{"disambiguationData":[OSD([sQuery(id+"F4.wireOp",EDGE,"E30")])]}),makeQuery(id+"F8.opExtrude","SWEPT_FACE",FACE,{"disambiguationData":[OSD([sQuery(id+"F7.wireOp",EDGE,"E67")])]})]});
            fillet(context, id + "F14", {"entities" : qUnion([Q0, Q1, Q2, Q3, Q4, Q5]), "radius" : 3 * mm, "tangentPropagation" : true, "allowEdgeOverflow" : false});
        }
        {
            var Q0;
            Q0=makeQuery(id+"F1.opExtrude","CAP_EDGE",EDGE,{"disambiguationData":[OSD([sQuery(id+"F0.wireOp",EDGE,"E1.bottom")])],"isStart":false});
            fillet(context, id + "F15", {"entities" : qUnion([Q0]), "radius" : 2 * mm, "tangentPropagation" : true, "allowEdgeOverflow" : false});
        }
        {
            var Q0;
            {var subQ0=sQuery(id+"F0.wireOp",EDGE,"E22.filletArc");var subQ1=sQuery(id+"F0.wireOp",EDGE,"E7");var subQ2=sQuery(id+"F0.wireOp",EDGE,"E6");var subQ3=sQuery(id+"F0.wireOp",EDGE,"E5");var subQ4=sQuery(id+"F0.wireOp",EDGE,"E4");var subQ5=sQuery(id+"F0.wireOp",EDGE,"E1.bottom");var subQ6=sQuery(id+"F0.wireOp",EDGE,"E21.filletArc");var subQ7=sQuery(id+"F0.wireOp",EDGE,"E1.top");var subQ8=sQuery(id+"F0.wireOp",EDGE,"E1.left");var subQ9=sQuery(id+"F0.wireOp",EDGE,"E1.right");var subQ10=sQuery(id+"F0.wireOp",EDGE,"E23.filletArc");var subQ11=sQuery(id+"F0.wireOp",EDGE,"E24.filletArc");Q0=makeQuery(id+"F2.boolean.opBoolean","SPLIT",FACE,{"disambiguationData":[TD([makeQuery(id+"F1.opExtrude","SWEPT_FACE",FACE,{"disambiguationData":[OSD([subQ5])]})])],"derivedFrom":makeQuery(id+"F1.opExtrude","CAP_FACE",FACE,{"disambiguationData":[OSD([subQ5,subQ7,subQ8,subQ9,subQ4,subQ3,subQ2,subQ1,subQ6,subQ0,subQ10,subQ11])],"isStart":true})});}
            var sketch = newSketch(context, id + "F16", { "sketchPlane" : qUnion([Q0])});
            skLineSegment(sketch, "E79", {"start": v(0, 74.25) * mm, "end": v(0, 104.25) * mm, "construction": true});
            skCircle(sketch, "E80", {"center": v(0, 104.25) * mm, "radius": 6 * mm});
            skArc(sketch, "E81", {"start": v(15, 103.81) * mm, "mid": v(0.01, 119.25) * mm, "end": v(-15, 103.84) * mm});
            skLineSegment(sketch, "E82", {"start": v(-15, 103.84) * mm, "end": v(-15, 92.25) * mm});
            skLineSegment(sketch, "E83", {"start": v(-15, 92.25) * mm, "end": v(-33, 74.25) * mm});
            skLineSegment(sketch, "E84", {"start": v(15, 103.81) * mm, "end": v(15, 93.3) * mm});
            skLineSegment(sketch, "E85", {"start": v(15, 93.3) * mm, "end": v(34.03, 74.25) * mm});
            skLineSegment(sketch, "E86", {"start": v(-74.25, 0) * mm, "end": v(74.25, 0) * mm, "construction": true});
            skLineSegment(sketch, "E87.MirrorCS", {"start": v(15, 92.25) * mm, "end": v(33, 74.25) * mm});
            skLineSegment(sketch, "E88.MirrorCS", {"start": v(-15, 93.3) * mm, "end": v(-34.03, 74.25) * mm});
            skLineSegment(sketch, "E89.MirrorCS", {"start": v(-15, 103.81) * mm, "end": v(-15, 93.3) * mm});
            skLineSegment(sketch, "E90.MirrorCS", {"start": v(15, 103.84) * mm, "end": v(15, 92.25) * mm});
            skArc(sketch, "E91.MirrorCS", {"start": v(-15, 103.81) * mm, "mid": v(-0.01, 119.25) * mm, "end": v(15, 103.84) * mm});
            skLineSegment(sketch, "E92.MirrorCS", {"start": v(-15, -92.25) * mm, "end": v(-33, -74.25) * mm});
            skLineSegment(sketch, "E93.MirrorCS", {"start": v(15, -93.3) * mm, "end": v(34.03, -74.25) * mm});
            skCircle(sketch, "E94.MirrorC", {"center": v(0, -104.25) * mm, "radius": 6 * mm});
            skLineSegment(sketch, "E95.MirrorCS", {"start": v(-15, -103.84) * mm, "end": v(-15, -92.25) * mm});
            skLineSegment(sketch, "E96.MirrorCS", {"start": v(15, -103.84) * mm, "end": v(15, -92.25) * mm});
            skLineSegment(sketch, "E97.MirrorCS", {"start": v(-15, -103.81) * mm, "end": v(-15, -93.3) * mm});
            skLineSegment(sketch, "E98.MirrorCS", {"start": v(15, -103.81) * mm, "end": v(15, -93.3) * mm});
            skArc(sketch, "E99.MirrorCS", {"start": v(-15, -103.81) * mm, "mid": v(-0.01, -119.25) * mm, "end": v(15, -103.84) * mm});
            skArc(sketch, "E100.MirrorCS", {"start": v(15, -103.81) * mm, "mid": v(0.01, -119.25) * mm, "end": v(-15, -103.84) * mm});
            skSolve(sketch);
        }
        {
            var Q0;
            {var subQ0=sQuery(id+"F16.wireOp",EDGE,"E84");Q0=makeQuery(id+"F16.imprint","IMPRINT",FACE,{"disambiguationData":[TD([[makeQuery(id+"F16.imprint","IMPRINT",EDGE,{"derivedFrom":subQ0}),1.0]])]});}
            var Q1;
            {var subQ0=sQuery(id+"F16.wireOp",EDGE,"E89.MirrorCS");Q1=makeQuery(id+"F16.imprint","IMPRINT",FACE,{"disambiguationData":[TD([[makeQuery(id+"F16.imprint","IMPRINT",EDGE,{"derivedFrom":subQ0}),-1.0]])]});}
            var Q2;
            {var subQ0=sQuery(id+"F16.wireOp",EDGE,"E98.MirrorCS");Q2=makeQuery(id+"F16.imprint","IMPRINT",FACE,{"disambiguationData":[TD([[makeQuery(id+"F16.imprint","IMPRINT",EDGE,{"derivedFrom":subQ0}),-1.0]])]});}
            var Q3;
            {var subQ1=sQuery(id+"F16.wireOp",EDGE,"E92.MirrorCS");Q3=makeQuery(id+"F16.imprint","IMPRINT",FACE,{"disambiguationData":[TD([[makeQuery(id+"F16.imprint","IMPRINT",EDGE,{"derivedFrom":subQ1}),-1.0]])]});}
            var Q4;
            Q4=makeQuery(id+"F16.imprint","IMPRINT",FACE,{"disambiguationData":[TD([[makeQuery(id+"F16.imprint","IMPRINT",EDGE,{"derivedFrom":makeQuery(id+"F1.opExtrude","CAP_EDGE",EDGE,{"disambiguationData":[OSD([sQuery(id+"F0.wireOp",EDGE,"E1.left")])],"isStart":true})}),-1.0]])]});
            var Q5;
            {var subQ3=sQuery(id+"F16.wireOp",EDGE,"E83");Q5=makeQuery(id+"F16.imprint","IMPRINT",FACE,{"disambiguationData":[TD([[makeQuery(id+"F16.imprint","IMPRINT",EDGE,{"derivedFrom":subQ3}),1.0]])]});}
            var Q6;
            Q6=makeQuery(id+"F2.opExtrude","CAP_FACE",FACE,{"disambiguationData":[OSD([sQuery(id+"F0.wireOp",EDGE,"E12"),sQuery(id+"F0.wireOp",EDGE,"E13"),sQuery(id+"F0.wireOp",EDGE,"E14"),sQuery(id+"F0.wireOp",EDGE,"E15"),sQuery(id+"F0.wireOp",EDGE,"E17.filletArc"),sQuery(id+"F0.wireOp",EDGE,"E18.filletArc"),sQuery(id+"F0.wireOp",EDGE,"E19.filletArc"),sQuery(id+"F0.wireOp",EDGE,"E20.filletArc"),sQuery(id+"F0.wireOp",EDGE,"E25.0"),sQuery(id+"F0.wireOp",EDGE,"E25.1"),sQuery(id+"F0.wireOp",EDGE,"E25.2"),sQuery(id+"F0.wireOp",EDGE,"E25.3"),sQuery(id+"F0.wireOp",EDGE,"E25.4"),sQuery(id+"F0.wireOp",EDGE,"E25.5"),sQuery(id+"F0.wireOp",EDGE,"E25.6"),sQuery(id+"F0.wireOp",EDGE,"E25.7")])],"isStart":false});
            extrude(context, id + "F17", {"entities" : qUnion([Q0, Q1, Q2, Q3, Q4, Q5]), "operationType" : NewBodyOperationType.ADD, "endBound" : BoundingType.UP_TO_SURFACE, "endBoundEntityFace" : qUnion([Q6]), "depth" : 25 * mm});
        }
    });
